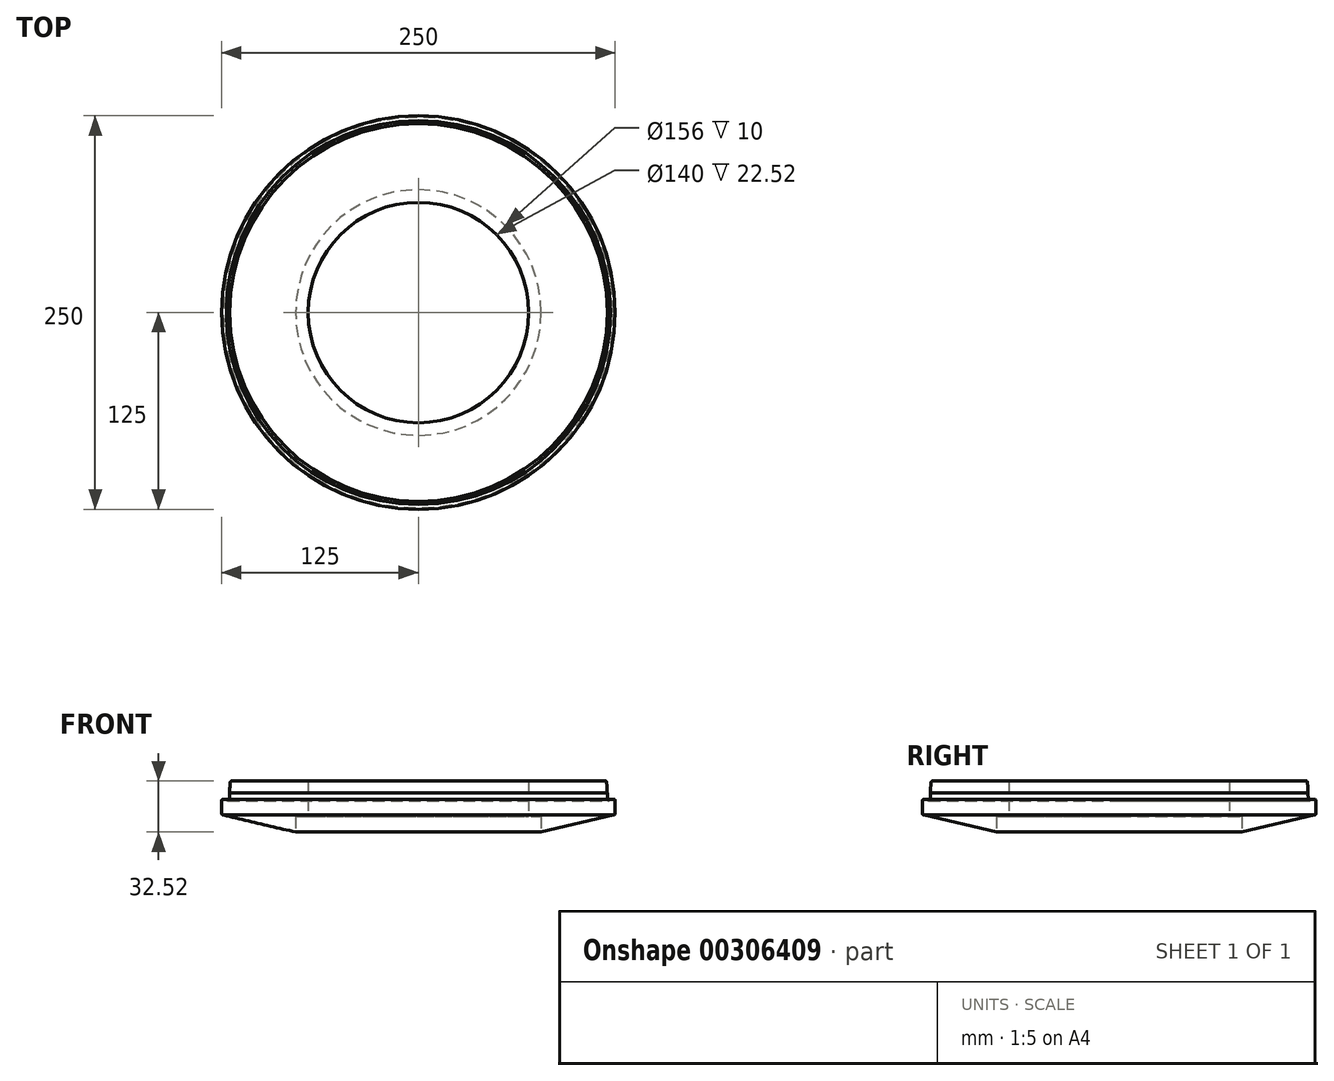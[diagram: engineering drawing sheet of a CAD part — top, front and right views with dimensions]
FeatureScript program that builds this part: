
annotation { "Feature Type Name" : "Feature", "Feature Type Description" : "" }
export const myFeature = defineFeature(function(context is Context, id is Id, definition is map)
    precondition{}
    {
        {
            var Q0;
            Q0=qCreatedBy(makeId("Front.planeOp"),FACE);
            var sketch = newSketch(context, id + "F0", { "sketchPlane" : qUnion([Q0])});
            skLineSegment(sketch, "E0.right", {"start": v(-125, 4) * mm, "end": v(-125, -4) * mm});
            skPoint(sketch, "E0.middle", {"position": v(0, 0) * mm});
            skLineSegment(sketch, "E1.top", {"start": v(-118.53, 16.6) * mm, "end": v(-70, 16.6) * mm});
            skLineSegment(sketch, "E1.right", {"start": v(0, 5) * mm, "end": v(0, 16.6) * mm});
            skPoint(sketch, "E2.endSnap0", {"position": v(0, -5) * mm});
            skArc(sketch, "E3", {"start": v(-119.93, 9) * mm, "mid": v(-119.77, 12.35) * mm, "end": v(-119.52, 15.69) * mm});
            skPoint(sketch, "E4.visualSharp", {"position": v(-125, -5) * mm});
            skArc(sketch, "E4.filletArc", {"start": v(-125, -4) * mm, "mid": v(-124.7, -4.7) * mm, "end": v(-124, -5) * mm});
            skArc(sketch, "E5.filletArc", {"start": v(-124, 5) * mm, "mid": v(-124.7, 4.7) * mm, "end": v(-125, 4) * mm});
            skPoint(sketch, "E0.left.start.orphan", {"position": v(125, 5) * mm});
            skPoint(sketch, "E6.visualSharp", {"position": v(-119.44, 16.6) * mm});
            skArc(sketch, "E6.filletArc", {"start": v(-118.53, 16.6) * mm, "mid": v(-119.2, 16.34) * mm, "end": v(-119.52, 15.69) * mm});
            skLineSegment(sketch, "E7", {"start": v(0, -5) * mm, "end": v(0, -15.92) * mm});
            skLineSegment(sketch, "E8", {"start": v(-78, -15.92) * mm, "end": v(-124, -5) * mm});
            skLineSegment(sketch, "E9", {"start": v(-78, -15.92) * mm, "end": v(-78, -5.92) * mm});
            skLineSegment(sketch, "E10", {"start": v(-70, -5.92) * mm, "end": v(-78, -5.92) * mm});
            skLineSegment(sketch, "E11", {"start": v(0, 5) * mm, "end": v(0, -5) * mm});
            skLineSegment(sketch, "E12", {"start": v(-78, -5.92) * mm, "end": v(-70, -5.92) * mm});
            skLineSegment(sketch, "E13", {"start": v(-70, -5.92) * mm, "end": v(-70, 16.6) * mm});
            skPoint(sketch, "E14.orphan", {"position": v(0, -5.92) * mm});
            skArc(sketch, "E15", {"start": v(-122, 5) * mm, "mid": v(-121, 4) * mm, "end": v(-120, 5) * mm});
            skLineSegment(sketch, "E16", {"start": v(-119.93, 9) * mm, "end": v(-120, 5) * mm});
            skLineSegment(sketch, "E17", {"start": v(-124, 5) * mm, "end": v(-122, 5) * mm});
            skSolve(sketch);
        }
        {
            var Q0;
            Q0=makeQuery(id+"F0.imprint","IMPRINT",FACE,{"disambiguationData":[TD([[makeQuery(id+"F0.imprint","IMPRINT",EDGE,{"derivedFrom":sQuery(id+"F0.wireOp",EDGE,"E0.right")}),1.0]])]});
            var Q1;
            Q1=sQuery(id+"F0.wireOp",EDGE,"E1.right");
            revolve(context, id + "F1", {"entities" : qUnion([Q0]), "axis" : qUnion([Q1]), "revolveType" : RevolveType.FULL});
        }
    });
